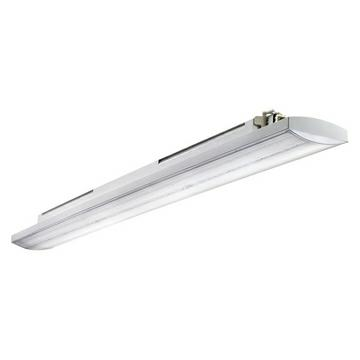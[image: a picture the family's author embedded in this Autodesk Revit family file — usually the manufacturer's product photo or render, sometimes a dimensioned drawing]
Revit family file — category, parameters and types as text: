
# Revit family: Lighting-Industriale-GEWISS-SMART[3]-PLAFONIERA-LED_TRASPARENTE_1200mm
name_source: partatom
category: Apparecchi per illuminazione
units: mm (PartAtom-declared; Revit-internal decimal feet)

## family parameters
Condiviso = No
Host = Superficie
Punto di calcolo locali = Sì
Quota connettore circolare = Usa diametro
Sorgente d'illuminazione = No
Taglio con vuoti quando caricato = No
Tipo di parte = Normale

## types (1)
- Lighting-Industriale-GEWISS-SMART[3]-PLAFONIERA-LED_TRASPARENTE_1200mm
    Apparecchio a ridotta temperatura superficiale = Conforme
    Applicazione = Interno
    Catalogo = LIGHTING
    Catalogo Serie = SMART [3]
    Classe di efficienza LED integrati = A ÷ A++
    Classe isolamento = II
    Codice EAN = 8011564876064
    Codice Electrocod = 2434
    Descrizione = SMART3 1200 63LED 43W TRASPARENTE CABLAGGIO PASSANTE 4000K
    Failure rate apparecchio (35.000h, Tq=35° C) = <2,5%
    Failure rate apparecchio (50.000h, Tq=25° C) = <2,5%
    Flusso nominale (lm) = 5500
    Ganci = GEWISS  - ALLUMINIO
    Garanzia = 5 anni
    Glow Wire Test = 850°C
    Grado di protezione = IP66/IP69
    IDF = 8913c65b-cf7b-4f0b-93b3-2bbdd1938487
    IDT = e9f9df53-c11c-4f09-88fd-a725bd6bd6c1
    Immagine tipo = GWS3136T.jpg
    LED Life time (L70) = 80000H
    LED Life time (L80B50) = 100000H
    LED Life time (L90B50) = 50000H
    LED LifeTime (L80B20) = 85000H
    Lampada = LED
    Lampada: = LED
    Lumen output (lm) = 4900
    Lunghezza = 1200 mm
    Lunghezza Lampada = 1200 mm
    Modello = GWS3236TL
    N° LED (#) = 63
    Peso (kg): = 2
    Potenza di sistema = 40W
    Produttore = GEWISS S.p.A.
    Prospetto di default = 1219 mm
    Resistenza agli urti = IK08
    SEO = Plafoniera
    Scheda Tecnica = https://www.gewiss.com
    Schermo = Trasparente
    Schermo- = Gewiss - Led Acceso
    Stampa 1_100 = Sì
    Stampa 1_200 = No
    Struttura = GEWISS - SMART 3 - GRIGIO
    Temperatura di colore = 4000 K (CRI 80)
    Temperatura di colore: = 4000 K (CRI 80)
    Temperatura di funzionamento = -25 +50 °C
    Temperatura di utilizzo = -30 +50 °C
    Tensione = 220/240 V - 50/60 Hz - Stand alone
    Tipo alimentatore = Driver Led in corrente continua
    Tipologia = Stand alone
    Tipologia sorgente luminosa = LED - Non sostituibile
    URL = https://www.gewiss.com
    Versione file RFA = 20.11
